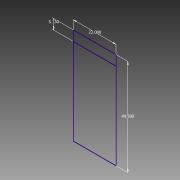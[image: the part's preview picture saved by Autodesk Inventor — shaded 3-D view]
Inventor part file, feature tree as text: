
AUTODESK INVENTOR PART (.ipt)
format: ipt  version: 2013 (Build 170138000, 138)  size: 61,952 bytes
history: native  units: in
note: dims shown in document units (in); Inventor stores cm internally (conversion verified against a paired STEP export)
features: sketch x1
ambient origin geometry x8: Origin, YZ Plane, XZ Plane, XY Plane, X Axis, Y Axis, Z Axis, Center Point
feature tree (1):
  sketch  "Sketch1"  dims[d0=22.0in d1=49.5in d2=5.13in]
